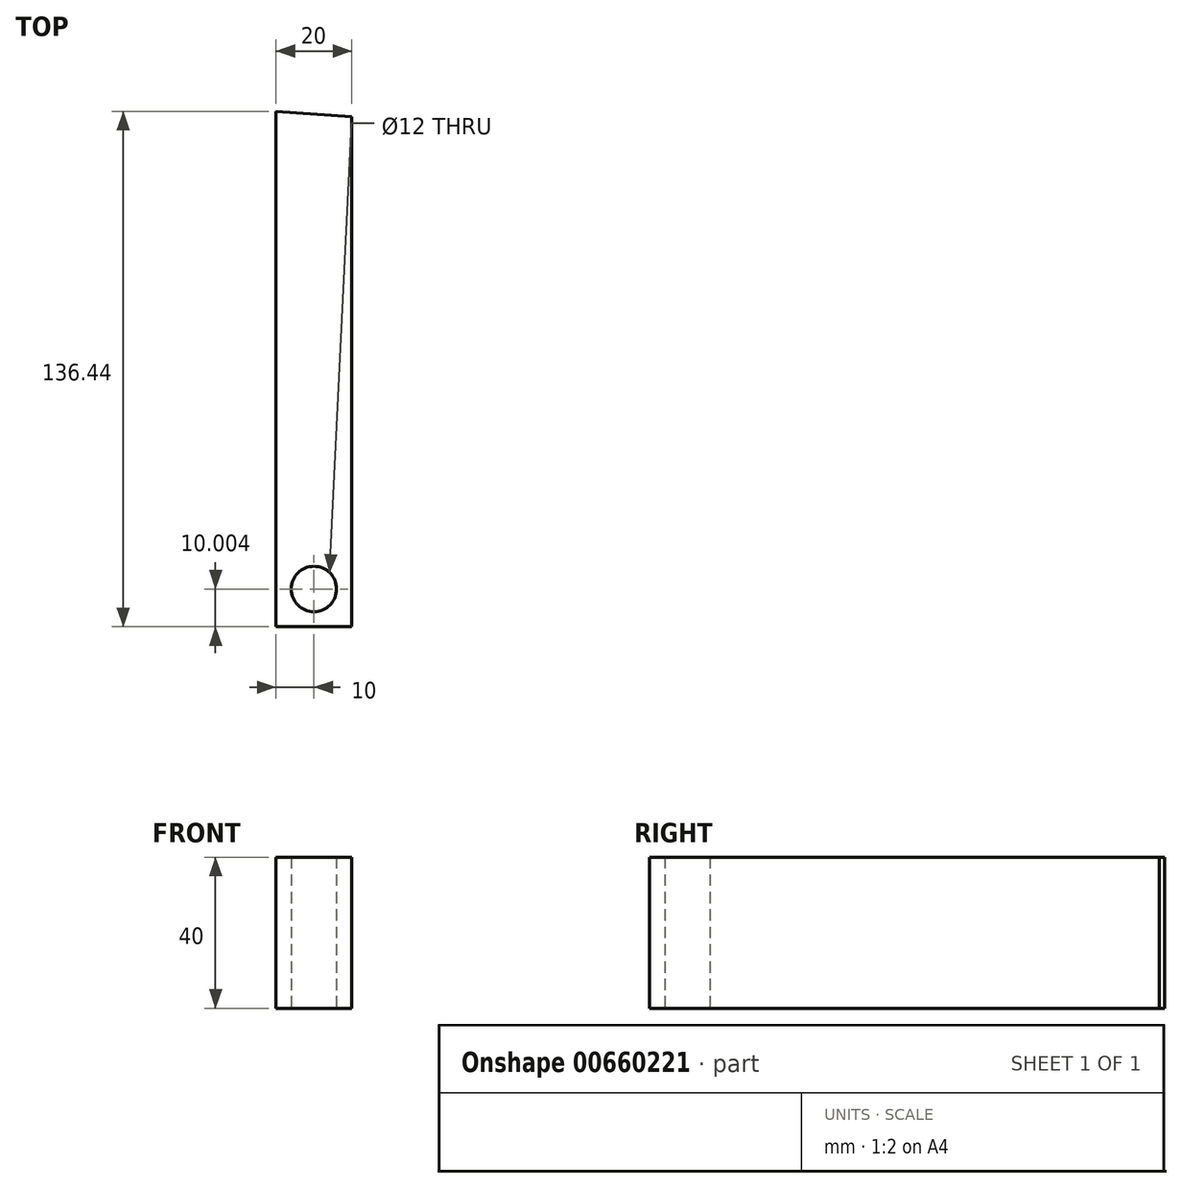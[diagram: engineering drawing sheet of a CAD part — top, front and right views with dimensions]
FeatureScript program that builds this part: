
annotation { "Feature Type Name" : "Feature", "Feature Type Description" : "" }
export const myFeature = defineFeature(function(context is Context, id is Id, definition is map)
    precondition{}
    {
        {
            var Q0;
            Q0=qCreatedBy(makeId("Top.planeOp"),FACE);
            var sketch = newSketch(context, id + "F0", { "sketchPlane" : qUnion([Q0])});
            skLineSegment(sketch, "E0.left", {"start": v(-510, -89.94) * mm, "end": v(-510, 26.5) * mm});
            skLineSegment(sketch, "E0.right", {"start": v(-490, -89.94) * mm, "end": v(-490, 25.06) * mm});
            skLineSegment(sketch, "E1.bottom", {"start": v(-510, -109.94) * mm, "end": v(-490, -109.94) * mm});
            skLineSegment(sketch, "E1.top", {"start": v(-510, -89.94) * mm, "end": v(-510, -89.94) * mm});
            skLineSegment(sketch, "E1.left", {"start": v(-510, -109.94) * mm, "end": v(-510, -89.94) * mm});
            skLineSegment(sketch, "E1.right", {"start": v(-490, -109.94) * mm, "end": v(-490, -89.94) * mm});
            skCircle(sketch, "E2", {"center": v(-500, -99.94) * mm, "radius": 6 * mm});
            skLineSegment(sketch, "E3.trimOffspring", {"start": v(-490, -89.94) * mm, "end": v(-490, -89.94) * mm});
            skPoint(sketch, "E4.start.orphan", {"position": v(-510, -109.94) * mm});
            skLineSegment(sketch, "E5", {"start": v(-510, 26.5) * mm, "end": v(-490, 25.06) * mm});
            skLineSegment(sketch, "E6", {"start": v(-500, -109.94) * mm, "end": v(-500, 25.78) * mm, "construction": true});
            skSolve(sketch);
        }
        {
            var Q0;
            Q0=qSketchRegion(id+"F0",true);
            extrude(context, id + "F1", {"entities" : qUnion([Q0]), "depth" : 40 * mm, "offsetDistance" : 25 * mm});
        }
    });
